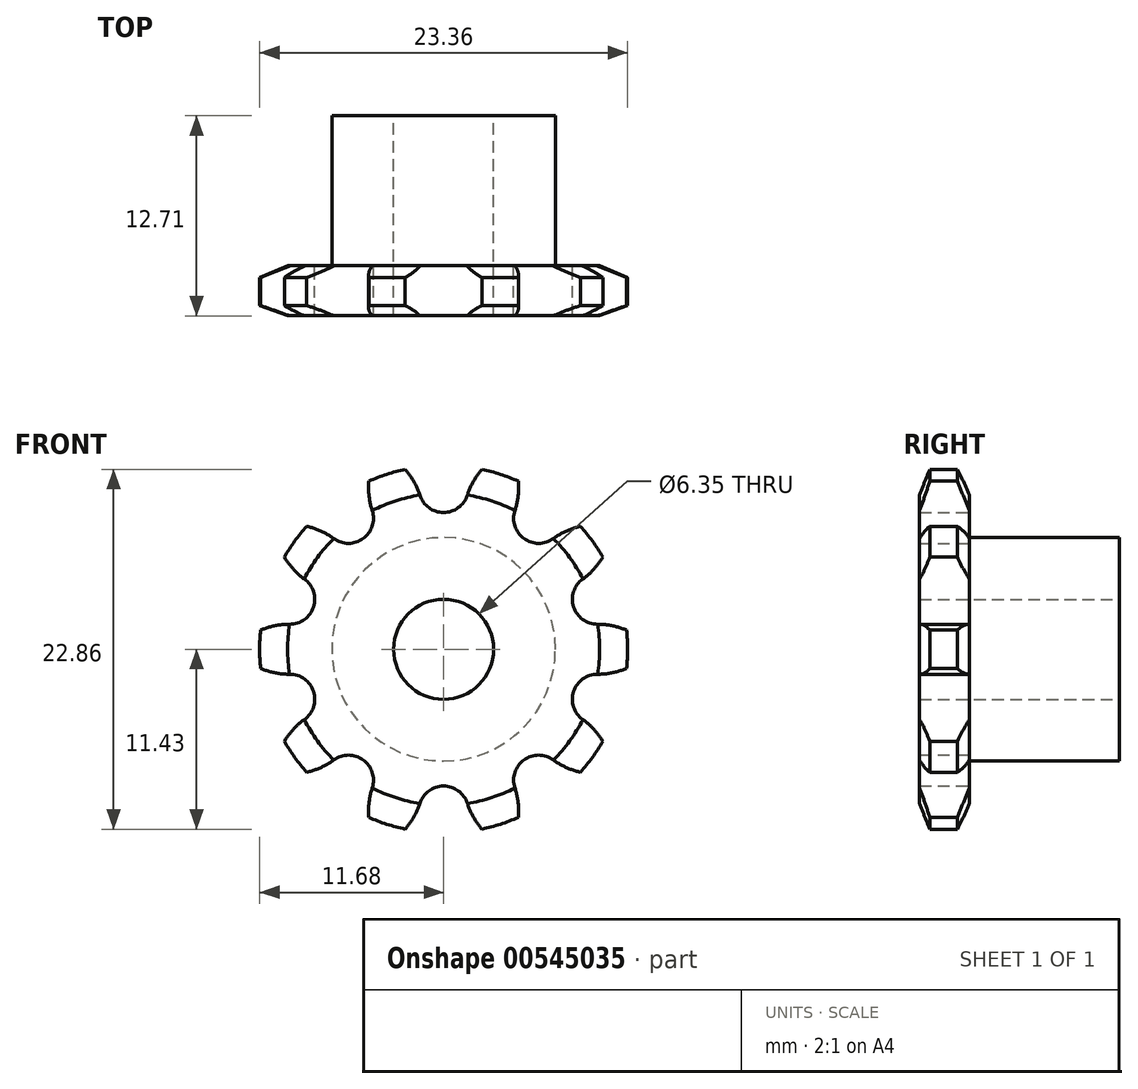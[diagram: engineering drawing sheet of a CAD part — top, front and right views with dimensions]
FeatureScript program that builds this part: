
annotation { "Feature Type Name" : "Feature", "Feature Type Description" : "" }
export const myFeature = defineFeature(function(context is Context, id is Id, definition is map)
    precondition{}
    {
        {
            var Q0;
            Q0=qCreatedBy(makeId("Front.planeOp"),FACE);
            var sketch = newSketch(context, id + "F0", { "sketchPlane" : qUnion([Q0])});
            skLineSegment(sketch, "E0.1", {"start": v(6.04, 8.31) * mm, "end": v(9.77, 3.17) * mm, "construction": true});
            skLineSegment(sketch, "E0.2", {"start": v(9.77, 3.17) * mm, "end": v(9.77, -3.17) * mm, "construction": true});
            skLineSegment(sketch, "E0.3", {"start": v(9.77, -3.17) * mm, "end": v(6.04, -8.31) * mm, "construction": true});
            skLineSegment(sketch, "E0.4", {"start": v(6.04, -8.31) * mm, "end": v(0, -10.27) * mm, "construction": true});
            skLineSegment(sketch, "E0.5", {"start": v(0, -10.27) * mm, "end": v(-6.04, -8.31) * mm, "construction": true});
            skLineSegment(sketch, "E0.6", {"start": v(-6.04, -8.31) * mm, "end": v(-9.77, -3.18) * mm, "construction": true});
            skLineSegment(sketch, "E0.7", {"start": v(-9.77, -3.18) * mm, "end": v(-9.77, 3.17) * mm, "construction": true});
            skLineSegment(sketch, "E0.8", {"start": v(-9.77, 3.17) * mm, "end": v(-6.04, 8.31) * mm, "construction": true});
            skLineSegment(sketch, "E0.9", {"start": v(-6.04, 8.31) * mm, "end": v(0, 10.27) * mm, "construction": true});
            skCircle(sketch, "E1", {"center": v(0, 0) * mm, "radius": 3.18 * mm});
            skCircle(sketch, "E2", {"center": v(6.04, 8.31) * mm, "radius": 1.59 * mm});
            skCircle(sketch, "E3", {"center": v(0, 10.27) * mm, "radius": 1.59 * mm});
            skCircle(sketch, "E4", {"center": v(-6.04, 8.31) * mm, "radius": 1.59 * mm});
            skCircle(sketch, "E5", {"center": v(-9.77, 3.17) * mm, "radius": 1.59 * mm});
            skCircle(sketch, "E6", {"center": v(6.04, -8.31) * mm, "radius": 1.59 * mm});
            skCircle(sketch, "E7", {"center": v(0, -10.27) * mm, "radius": 1.59 * mm});
            skCircle(sketch, "E8", {"center": v(-9.77, -3.18) * mm, "radius": 1.59 * mm});
            skCircle(sketch, "E9", {"center": v(-6.04, -8.31) * mm, "radius": 1.59 * mm});
            skCircle(sketch, "E10", {"center": v(9.77, -3.17) * mm, "radius": 1.59 * mm});
            skCircle(sketch, "E11", {"center": v(9.77, 3.17) * mm, "radius": 1.59 * mm});
            skArc(sketch, "E12", {"start": v(1.5, 9.78) * mm, "mid": v(2.5, 11.5) * mm, "end": v(4.12, 12.67) * mm});
            skArc(sketch, "E13", {"start": v(4.53, 8.8) * mm, "mid": v(4.74, 10.78) * mm, "end": v(4.12, 12.67) * mm});
            skArc(sketch, "E14", {"start": v(6.97, 7.03) * mm, "mid": v(8.79, 7.84) * mm, "end": v(10.78, 7.83) * mm});
            skArc(sketch, "E15", {"start": v(8.84, 4.46) * mm, "mid": v(10.17, 5.94) * mm, "end": v(10.78, 7.83) * mm});
            skArc(sketch, "E16", {"start": v(9.77, 1.59) * mm, "mid": v(11.72, 1.17) * mm, "end": v(13.32, 0) * mm});
            skArc(sketch, "E17", {"start": v(9.77, -1.59) * mm, "mid": v(11.72, -1.17) * mm, "end": v(13.32, 0) * mm});
            skArc(sketch, "E18", {"start": v(8.84, -4.46) * mm, "mid": v(10.17, -5.94) * mm, "end": v(10.78, -7.83) * mm});
            skArc(sketch, "E19", {"start": v(6.97, -7.03) * mm, "mid": v(8.79, -7.84) * mm, "end": v(10.78, -7.83) * mm});
            skArc(sketch, "E20", {"start": v(1.5, -9.78) * mm, "mid": v(2.5, -11.5) * mm, "end": v(4.12, -12.67) * mm});
            skArc(sketch, "E21", {"start": v(4.53, -8.8) * mm, "mid": v(4.74, -10.78) * mm, "end": v(4.12, -12.67) * mm});
            skArc(sketch, "E22", {"start": v(-4.53, -8.8) * mm, "mid": v(-4.74, -10.78) * mm, "end": v(-4.12, -12.67) * mm});
            skArc(sketch, "E23", {"start": v(-1.5, -9.78) * mm, "mid": v(-2.5, -11.5) * mm, "end": v(-4.12, -12.67) * mm});
            skArc(sketch, "E24", {"start": v(-8.84, -4.46) * mm, "mid": v(-10.17, -5.94) * mm, "end": v(-10.78, -7.83) * mm});
            skArc(sketch, "E25", {"start": v(-6.97, -7.03) * mm, "mid": v(-8.79, -7.84) * mm, "end": v(-10.78, -7.83) * mm});
            skArc(sketch, "E26", {"start": v(-9.77, 1.59) * mm, "mid": v(-11.72, 1.17) * mm, "end": v(-13.32, 0) * mm});
            skArc(sketch, "E27", {"start": v(-9.77, -1.59) * mm, "mid": v(-11.72, -1.17) * mm, "end": v(-13.32, 0) * mm});
            skArc(sketch, "E28", {"start": v(-6.97, 7.03) * mm, "mid": v(-8.79, 7.84) * mm, "end": v(-10.78, 7.83) * mm});
            skArc(sketch, "E29", {"start": v(-8.84, 4.46) * mm, "mid": v(-10.17, 5.94) * mm, "end": v(-10.78, 7.83) * mm});
            skArc(sketch, "E30", {"start": v(-1.5, 9.78) * mm, "mid": v(-2.5, 11.5) * mm, "end": v(-4.12, 12.67) * mm});
            skArc(sketch, "E31", {"start": v(-4.53, 8.8) * mm, "mid": v(-4.74, 10.78) * mm, "end": v(-4.12, 12.67) * mm});
            skCircle(sketch, "E32", {"center": v(0, 0) * mm, "radius": 11.68 * mm});
            skLineSegment(sketch, "E33", {"start": v(0, 0) * mm, "end": v(0, 15.73) * mm, "construction": true});
            skPoint(sketch, "E34.endSnap0", {"position": v(-9.77, 0) * mm});
            skCircle(sketch, "E35", {"center": v(0, 0) * mm, "radius": 10.27 * mm, "construction": true});
            skLineSegment(sketch, "E36", {"start": v(0, 10.27) * mm, "end": v(6.04, 8.31) * mm, "construction": true});
            skCircle(sketch, "E37", {"center": v(0, 0) * mm, "radius": 7.1 * mm});
            skSolve(sketch);
        }
        {
            var Q0;
            Q0=makeQuery(id+"F0.imprint","IMPRINT",FACE,{"disambiguationData":[TD([[makeQuery(id+"F0.imprint","IMPRINT",EDGE,{"derivedFrom":sQuery(id+"F0.wireOp",EDGE,"E1")}),-1.0]])]});
            var Q1;
            Q1=makeQuery(id+"F0.imprint","IMPRINT",FACE,{"disambiguationData":[TD([[makeQuery(id+"F0.imprint","IMPRINT",EDGE,{"derivedFrom":sQuery(id+"F0.wireOp",EDGE,"E37")}),-1.0]])]});
            extrude(context, id + "F1", {"entities" : qUnion([Q0, Q1]), "depth" : 3.17 * mm, "offsetDistance" : 25.4 * mm});
        }
        {
            var Q0;
            Q0=makeQuery(id+"F0.imprint","IMPRINT",FACE,{"disambiguationData":[TD([[makeQuery(id+"F0.imprint","IMPRINT",EDGE,{"derivedFrom":sQuery(id+"F0.wireOp",EDGE,"E1")}),-1.0]])]});
            extrude(context, id + "F2", {"entities" : qUnion([Q0]), "operationType" : NewBodyOperationType.ADD, "oppositeDirection" : true, "depth" : 9.52 * mm, "offsetDistance" : 25.4 * mm});
        }
        {
            var Q0;
            {var subQ0=sQuery(id+"F0.wireOp",EDGE,"E32");Q0=makeQuery(id+"F1.opExtrude","CAP_EDGE",EDGE,{"disambiguationData":[OSD([subQ0]),TDD([makeQuery(id+"F0.imprint","IMPRINT",EDGE,{"disambiguationData":[TD([[makeQuery(id+"F0.imprint","INTERSECT",VERTEX,{"derivedFrom":[sQuery(id+"F0.wireOp",EDGE,"E30"),subQ0]}),-1.0]])],"derivedFrom":subQ0})])],"isStart":false});}
            var Q1;
            {var subQ0=sQuery(id+"F0.wireOp",EDGE,"E32");Q1=makeQuery(id+"F1.opExtrude","CAP_EDGE",EDGE,{"disambiguationData":[OSD([subQ0]),TDD([makeQuery(id+"F0.imprint","IMPRINT",EDGE,{"disambiguationData":[TD([[makeQuery(id+"F0.imprint","INTERSECT",VERTEX,{"derivedFrom":[sQuery(id+"F0.wireOp",EDGE,"E12"),subQ0]}),1.0]])],"derivedFrom":subQ0})])],"isStart":false});}
            var Q2;
            {var subQ0=sQuery(id+"F0.wireOp",EDGE,"E32");Q2=makeQuery(id+"F1.opExtrude","CAP_EDGE",EDGE,{"disambiguationData":[OSD([subQ0]),TDD([makeQuery(id+"F0.imprint","IMPRINT",EDGE,{"disambiguationData":[TD([[makeQuery(id+"F0.imprint","INTERSECT",VERTEX,{"derivedFrom":[sQuery(id+"F0.wireOp",EDGE,"E14"),subQ0]}),1.0]])],"derivedFrom":subQ0})])],"isStart":false});}
            var Q3;
            {var subQ0=sQuery(id+"F0.wireOp",EDGE,"E32");Q3=makeQuery(id+"F1.opExtrude","CAP_EDGE",EDGE,{"disambiguationData":[OSD([subQ0]),TDD([makeQuery(id+"F0.imprint","IMPRINT",EDGE,{"disambiguationData":[TD([[makeQuery(id+"F0.imprint","INTERSECT",VERTEX,{"derivedFrom":[sQuery(id+"F0.wireOp",EDGE,"E16"),subQ0]}),1.0]])],"derivedFrom":subQ0})])],"isStart":false});}
            var Q4;
            {var subQ0=sQuery(id+"F0.wireOp",EDGE,"E32");Q4=makeQuery(id+"F1.opExtrude","CAP_EDGE",EDGE,{"disambiguationData":[OSD([subQ0]),TDD([makeQuery(id+"F0.imprint","IMPRINT",EDGE,{"disambiguationData":[TD([[makeQuery(id+"F0.imprint","INTERSECT",VERTEX,{"derivedFrom":[sQuery(id+"F0.wireOp",EDGE,"E18"),subQ0]}),1.0]])],"derivedFrom":subQ0})])],"isStart":false});}
            var Q5;
            {var subQ0=sQuery(id+"F0.wireOp",EDGE,"E32");Q5=makeQuery(id+"F1.opExtrude","CAP_EDGE",EDGE,{"disambiguationData":[OSD([subQ0]),TDD([makeQuery(id+"F0.imprint","IMPRINT",EDGE,{"disambiguationData":[TD([[makeQuery(id+"F0.imprint","INTERSECT",VERTEX,{"derivedFrom":[sQuery(id+"F0.wireOp",EDGE,"E20"),subQ0]}),-1.0]])],"derivedFrom":subQ0})])],"isStart":false});}
            var Q6;
            {var subQ0=sQuery(id+"F0.wireOp",EDGE,"E32");Q6=makeQuery(id+"F1.opExtrude","CAP_EDGE",EDGE,{"disambiguationData":[OSD([subQ0]),TDD([makeQuery(id+"F0.imprint","IMPRINT",EDGE,{"disambiguationData":[TD([[makeQuery(id+"F0.imprint","INTERSECT",VERTEX,{"derivedFrom":[sQuery(id+"F0.wireOp",EDGE,"E22"),subQ0]}),-1.0]])],"derivedFrom":subQ0})])],"isStart":false});}
            var Q7;
            {var subQ0=sQuery(id+"F0.wireOp",EDGE,"E32");Q7=makeQuery(id+"F1.opExtrude","CAP_EDGE",EDGE,{"disambiguationData":[OSD([subQ0]),TDD([makeQuery(id+"F0.imprint","IMPRINT",EDGE,{"disambiguationData":[TD([[makeQuery(id+"F0.imprint","INTERSECT",VERTEX,{"derivedFrom":[sQuery(id+"F0.wireOp",EDGE,"E24"),subQ0]}),-1.0]])],"derivedFrom":subQ0})])],"isStart":false});}
            var Q8;
            {var subQ0=sQuery(id+"F0.wireOp",EDGE,"E32");Q8=makeQuery(id+"F1.opExtrude","CAP_EDGE",EDGE,{"disambiguationData":[OSD([subQ0]),TDD([makeQuery(id+"F0.imprint","IMPRINT",EDGE,{"disambiguationData":[TD([[makeQuery(id+"F0.imprint","INTERSECT",VERTEX,{"derivedFrom":[sQuery(id+"F0.wireOp",EDGE,"E26"),subQ0]}),-1.0]])],"derivedFrom":subQ0})])],"isStart":false});}
            var Q9;
            {var subQ0=sQuery(id+"F0.wireOp",EDGE,"E32");Q9=makeQuery(id+"F1.opExtrude","CAP_EDGE",EDGE,{"disambiguationData":[OSD([subQ0]),TDD([makeQuery(id+"F0.imprint","IMPRINT",EDGE,{"disambiguationData":[TD([[makeQuery(id+"F0.imprint","INTERSECT",VERTEX,{"derivedFrom":[sQuery(id+"F0.wireOp",EDGE,"E28"),subQ0]}),-1.0]])],"derivedFrom":subQ0})])],"isStart":false});}
            chamfer(context, id + "F3", {"entities" : qUnion([Q0, Q1, Q2, Q3, Q4, Q5, Q6, Q7, Q8, Q9]), "chamferType" : ChamferType.OFFSET_ANGLE, "width" : 1.78 * mm, "oppositeDirection" : false, "angle" : 20 * degree, "tangentPropagation" : true});
        }
        {
            var Q0;
            {var subQ0=sQuery(id+"F0.wireOp",EDGE,"E32");Q0=makeQuery(id+"F1.opExtrude","CAP_EDGE",EDGE,{"disambiguationData":[OSD([subQ0]),TDD([makeQuery(id+"F0.imprint","IMPRINT",EDGE,{"disambiguationData":[TD([[makeQuery(id+"F0.imprint","INTERSECT",VERTEX,{"derivedFrom":[sQuery(id+"F0.wireOp",EDGE,"E18"),subQ0]}),1.0]])],"derivedFrom":subQ0})])],"isStart":true});}
            var Q1;
            {var subQ0=sQuery(id+"F0.wireOp",EDGE,"E32");Q1=makeQuery(id+"F1.opExtrude","CAP_EDGE",EDGE,{"disambiguationData":[OSD([subQ0]),TDD([makeQuery(id+"F0.imprint","IMPRINT",EDGE,{"disambiguationData":[TD([[makeQuery(id+"F0.imprint","INTERSECT",VERTEX,{"derivedFrom":[sQuery(id+"F0.wireOp",EDGE,"E16"),subQ0]}),1.0]])],"derivedFrom":subQ0})])],"isStart":true});}
            var Q2;
            {var subQ0=sQuery(id+"F0.wireOp",EDGE,"E32");Q2=makeQuery(id+"F1.opExtrude","CAP_EDGE",EDGE,{"disambiguationData":[OSD([subQ0]),TDD([makeQuery(id+"F0.imprint","IMPRINT",EDGE,{"disambiguationData":[TD([[makeQuery(id+"F0.imprint","INTERSECT",VERTEX,{"derivedFrom":[sQuery(id+"F0.wireOp",EDGE,"E14"),subQ0]}),1.0]])],"derivedFrom":subQ0})])],"isStart":true});}
            var Q3;
            {var subQ0=sQuery(id+"F0.wireOp",EDGE,"E32");Q3=makeQuery(id+"F1.opExtrude","CAP_EDGE",EDGE,{"disambiguationData":[OSD([subQ0]),TDD([makeQuery(id+"F0.imprint","IMPRINT",EDGE,{"disambiguationData":[TD([[makeQuery(id+"F0.imprint","INTERSECT",VERTEX,{"derivedFrom":[sQuery(id+"F0.wireOp",EDGE,"E12"),subQ0]}),1.0]])],"derivedFrom":subQ0})])],"isStart":true});}
            var Q4;
            {var subQ0=sQuery(id+"F0.wireOp",EDGE,"E32");Q4=makeQuery(id+"F1.opExtrude","CAP_EDGE",EDGE,{"disambiguationData":[OSD([subQ0]),TDD([makeQuery(id+"F0.imprint","IMPRINT",EDGE,{"disambiguationData":[TD([[makeQuery(id+"F0.imprint","INTERSECT",VERTEX,{"derivedFrom":[sQuery(id+"F0.wireOp",EDGE,"E20"),subQ0]}),-1.0]])],"derivedFrom":subQ0})])],"isStart":true});}
            var Q5;
            {var subQ0=sQuery(id+"F0.wireOp",EDGE,"E32");Q5=makeQuery(id+"F1.opExtrude","CAP_EDGE",EDGE,{"disambiguationData":[OSD([subQ0]),TDD([makeQuery(id+"F0.imprint","IMPRINT",EDGE,{"disambiguationData":[TD([[makeQuery(id+"F0.imprint","INTERSECT",VERTEX,{"derivedFrom":[sQuery(id+"F0.wireOp",EDGE,"E22"),subQ0]}),-1.0]])],"derivedFrom":subQ0})])],"isStart":true});}
            var Q6;
            {var subQ0=sQuery(id+"F0.wireOp",EDGE,"E32");Q6=makeQuery(id+"F1.opExtrude","CAP_EDGE",EDGE,{"disambiguationData":[OSD([subQ0]),TDD([makeQuery(id+"F0.imprint","IMPRINT",EDGE,{"disambiguationData":[TD([[makeQuery(id+"F0.imprint","INTERSECT",VERTEX,{"derivedFrom":[sQuery(id+"F0.wireOp",EDGE,"E24"),subQ0]}),-1.0]])],"derivedFrom":subQ0})])],"isStart":true});}
            var Q7;
            {var subQ0=sQuery(id+"F0.wireOp",EDGE,"E32");Q7=makeQuery(id+"F1.opExtrude","CAP_EDGE",EDGE,{"disambiguationData":[OSD([subQ0]),TDD([makeQuery(id+"F0.imprint","IMPRINT",EDGE,{"disambiguationData":[TD([[makeQuery(id+"F0.imprint","INTERSECT",VERTEX,{"derivedFrom":[sQuery(id+"F0.wireOp",EDGE,"E26"),subQ0]}),-1.0]])],"derivedFrom":subQ0})])],"isStart":true});}
            var Q8;
            {var subQ0=sQuery(id+"F0.wireOp",EDGE,"E32");Q8=makeQuery(id+"F1.opExtrude","CAP_EDGE",EDGE,{"disambiguationData":[OSD([subQ0]),TDD([makeQuery(id+"F0.imprint","IMPRINT",EDGE,{"disambiguationData":[TD([[makeQuery(id+"F0.imprint","INTERSECT",VERTEX,{"derivedFrom":[sQuery(id+"F0.wireOp",EDGE,"E28"),subQ0]}),-1.0]])],"derivedFrom":subQ0})])],"isStart":true});}
            var Q9;
            {var subQ0=sQuery(id+"F0.wireOp",EDGE,"E32");Q9=makeQuery(id+"F1.opExtrude","CAP_EDGE",EDGE,{"disambiguationData":[OSD([subQ0]),TDD([makeQuery(id+"F0.imprint","IMPRINT",EDGE,{"disambiguationData":[TD([[makeQuery(id+"F0.imprint","INTERSECT",VERTEX,{"derivedFrom":[sQuery(id+"F0.wireOp",EDGE,"E30"),subQ0]}),-1.0]])],"derivedFrom":subQ0})])],"isStart":true});}
            chamfer(context, id + "F4", {"entities" : qUnion([Q0, Q1, Q2, Q3, Q4, Q5, Q6, Q7, Q8, Q9]), "chamferType" : ChamferType.OFFSET_ANGLE, "width" : 0.76 * mm, "oppositeDirection" : false, "angle" : 67 * degree, "tangentPropagation" : true});
        }
    });
